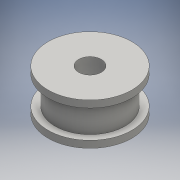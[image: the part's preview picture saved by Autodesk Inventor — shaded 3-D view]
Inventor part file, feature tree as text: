
AUTODESK INVENTOR PART (.ipt)
format: ipt  version: 2016 (Build 200138000, 138)  size: 118,784 bytes
history: native  units: mm
features: sketch x5, extrude x4
ambient origin geometry x8: Origin, YZ Plane, XZ Plane, XY Plane, X Axis, Y Axis, Z Axis, Center Point
bodies: Solid1 (feature_tree)
feature tree (9):
  extrude  "Extrusion1"  Depth=6.5mm
  extrude  "Extrusion2"  Depth=12.0mm
  sketch  "Sketch3"  dims[d5=2.0mm d6=0.0mm d7=6.5mm]
  extrude  "Extrusion3"  Depth=2.0mm
  extrude  "Extrusion4"  Depth=2.0mm TaperAngle=0.0deg
  sketch  "Sketch5"  dims[d11=2.0mm d12=0.0mm]
  sketch  "Sketch1"  dims[d0=20.0mm d1=6.5mm]
  sketch  "Sketch2"  dims[d2=12.0mm d3=0.0mm d4=24.0mm]
  sketch  "Sketch4"  dims[d8=24.0mm d9=2.0mm d10=0.0mm]
